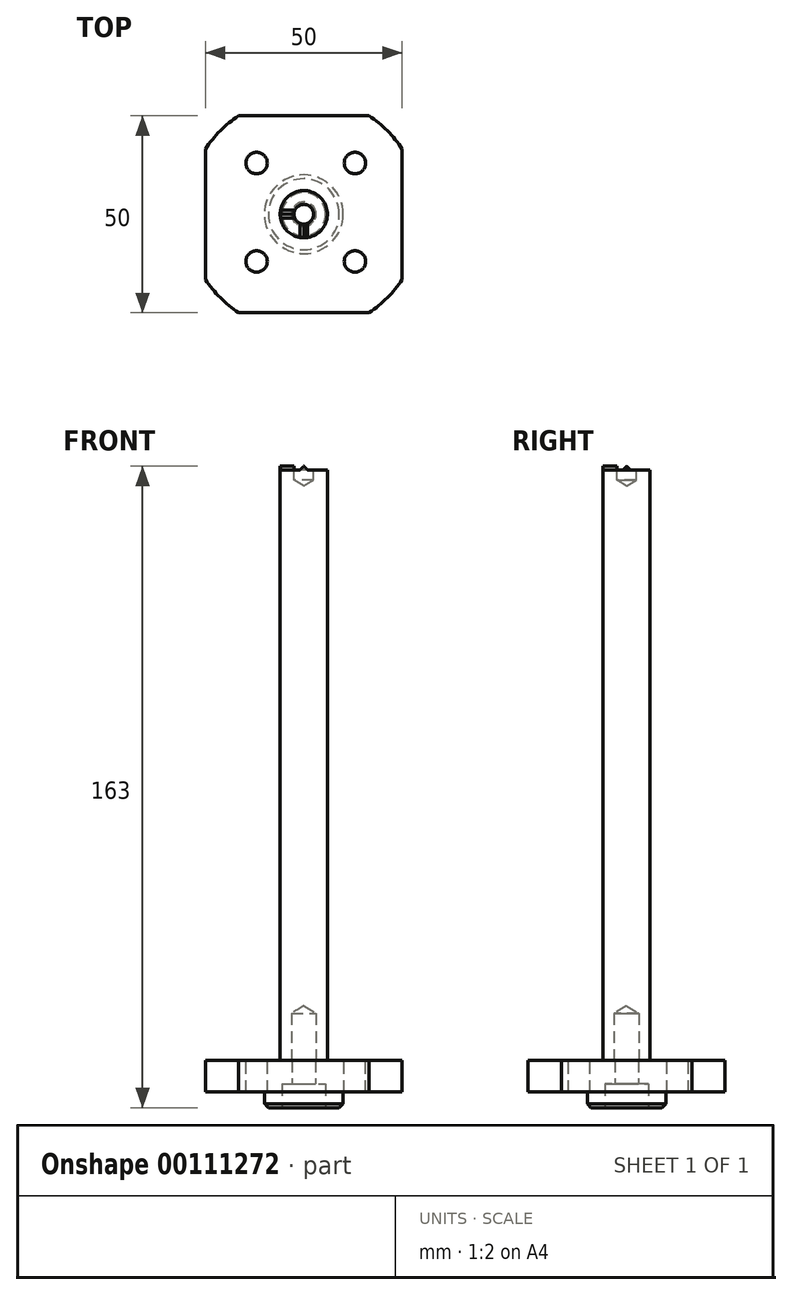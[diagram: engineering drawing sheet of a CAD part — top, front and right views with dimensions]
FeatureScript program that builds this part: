
annotation { "Feature Type Name" : "Feature", "Feature Type Description" : "" }
export const myFeature = defineFeature(function(context is Context, id is Id, definition is map)
    precondition{}
    {
        {
            var Q0;
            Q0=qCreatedBy(makeId("Top.planeOp"),FACE);
            var sketch = newSketch(context, id + "F0", { "sketchPlane" : qUnion([Q0])});
            skLineSegment(sketch, "E0.bottom", {"start": v(-25, 25) * mm, "end": v(25, 25) * mm});
            skLineSegment(sketch, "E0.top", {"start": v(-25, -25) * mm, "end": v(25, -25) * mm});
            skLineSegment(sketch, "E0.left", {"start": v(-25, 25) * mm, "end": v(-25, -25) * mm});
            skLineSegment(sketch, "E0.right", {"start": v(25, 25) * mm, "end": v(25, -25) * mm});
            skLineSegment(sketch, "E1", {"start": v(-25, 25) * mm, "end": v(25, -25) * mm, "construction": true});
            skLineSegment(sketch, "E2", {"start": v(25, 25) * mm, "end": v(-25, -25) * mm, "construction": true});
            skPoint(sketch, "E3", {"position": v(0, 0) * mm});
            skSolve(sketch);
        }
        {
            var Q0;
            Q0=makeQuery(id+"F0.imprint","IMPRINT",FACE,{"disambiguationData":[TD([[makeQuery(id+"F0.imprint","IMPRINT",EDGE,{"derivedFrom":sQuery(id+"F0.wireOp",EDGE,"E0.bottom")}),-1.0]])]});
            extrude(context, id + "F1", {"entities" : qUnion([Q0]), "depth" : 8 * mm});
        }
        {
            var Q0;
            Q0=makeQuery(id+"F1.opExtrude","CAP_FACE",FACE,{"disambiguationData":[OSD([sQuery(id+"F0.wireOp",EDGE,"E0.bottom"),sQuery(id+"F0.wireOp",EDGE,"E0.top"),sQuery(id+"F0.wireOp",EDGE,"E0.left"),sQuery(id+"F0.wireOp",EDGE,"E0.right")])],"isStart":true});
            var sketch = newSketch(context, id + "F2", { "sketchPlane" : qUnion([Q0])});
            skCircle(sketch, "E4", {"center": v(0, 0) * mm, "radius": 10 * mm});
            skSolve(sketch);
        }
        {
            var Q0;
            Q0=makeQuery(id+"F2.imprint","IMPRINT",FACE,{"disambiguationData":[TD([[makeQuery(id+"F2.imprint","IMPRINT",EDGE,{"derivedFrom":sQuery(id+"F2.wireOp",EDGE,"E4")}),1.0]])]});
            extrude(context, id + "F3", {"entities" : qUnion([Q0]), "operationType" : NewBodyOperationType.ADD, "depth" : 4 * mm});
        }
        {
            var Q0;
            Q0=makeQuery(id+"F1.opExtrude","CAP_FACE",FACE,{"disambiguationData":[OSD([sQuery(id+"F0.wireOp",EDGE,"E0.bottom"),sQuery(id+"F0.wireOp",EDGE,"E0.top"),sQuery(id+"F0.wireOp",EDGE,"E0.left"),sQuery(id+"F0.wireOp",EDGE,"E0.right")])],"isStart":false});
            var sketch = newSketch(context, id + "F4", { "sketchPlane" : qUnion([Q0])});
            skCircle(sketch, "E5", {"center": v(0, 0) * mm, "radius": 30 * mm});
            skCircle(sketch, "E6", {"center": v(0, 0) * mm, "radius": 6 * mm});
            skSolve(sketch);
        }
        {
            var Q0;
            {var subQ0=sQuery(id+"F4.wireOp",EDGE,"E5");var subQ1=makeQuery(id+"F1.opExtrude","CAP_EDGE",EDGE,{"disambiguationData":[OSD([sQuery(id+"F0.wireOp",EDGE,"E0.bottom")])],"isStart":false});var subQ2=makeQuery(id+"F4.imprint","INTERSECT",VERTEX,{"disambiguationData":[OD(1.0)],"derivedFrom":[subQ1,subQ0]});Q0=makeQuery(id+"F4.imprint","IMPRINT",FACE,{"disambiguationData":[TD([[makeQuery(id+"F4.imprint","IMPRINT",EDGE,{"disambiguationData":[TD([[subQ2,-1.0]])],"derivedFrom":subQ0}),-1.0]])]});}
            var Q1;
            {var subQ0=sQuery(id+"F4.wireOp",EDGE,"E5");var subQ1=makeQuery(id+"F1.opExtrude","CAP_EDGE",EDGE,{"disambiguationData":[OSD([sQuery(id+"F0.wireOp",EDGE,"E0.bottom")])],"isStart":false});var subQ2=makeQuery(id+"F4.imprint","INTERSECT",VERTEX,{"disambiguationData":[OD(0.0)],"derivedFrom":[subQ1,subQ0]});Q1=makeQuery(id+"F4.imprint","IMPRINT",FACE,{"disambiguationData":[TD([[makeQuery(id+"F4.imprint","IMPRINT",EDGE,{"disambiguationData":[TD([[subQ2,1.0]])],"derivedFrom":subQ0}),-1.0]])]});}
            var Q2;
            {var subQ0=sQuery(id+"F4.wireOp",EDGE,"E5");var subQ1=makeQuery(id+"F1.opExtrude","CAP_EDGE",EDGE,{"disambiguationData":[OSD([sQuery(id+"F0.wireOp",EDGE,"E0.top")])],"isStart":false});var subQ2=makeQuery(id+"F4.imprint","INTERSECT",VERTEX,{"disambiguationData":[OD(1.0)],"derivedFrom":[subQ1,subQ0]});Q2=makeQuery(id+"F4.imprint","IMPRINT",FACE,{"disambiguationData":[TD([[makeQuery(id+"F4.imprint","IMPRINT",EDGE,{"disambiguationData":[TD([[subQ2,-1.0]])],"derivedFrom":subQ0}),-1.0]])]});}
            var Q3;
            {var subQ0=sQuery(id+"F4.wireOp",EDGE,"E5");var subQ1=makeQuery(id+"F1.opExtrude","CAP_EDGE",EDGE,{"disambiguationData":[OSD([sQuery(id+"F0.wireOp",EDGE,"E0.left")])],"isStart":false});var subQ2=makeQuery(id+"F4.imprint","INTERSECT",VERTEX,{"disambiguationData":[OD(1.0)],"derivedFrom":[subQ1,subQ0]});Q3=makeQuery(id+"F4.imprint","IMPRINT",FACE,{"disambiguationData":[TD([[makeQuery(id+"F4.imprint","IMPRINT",EDGE,{"disambiguationData":[TD([[subQ2,-1.0]])],"derivedFrom":subQ0}),-1.0]])]});}
            extrude(context, id + "F5", {"entities" : qUnion([Q0, Q1, Q2, Q3]), "operationType" : NewBodyOperationType.REMOVE, "oppositeDirection" : true, "depth" : 25 * mm});
        }
        {
            var Q0;
            Q0=makeQuery(id+"F4.imprint","IMPRINT",FACE,{"disambiguationData":[TD([[makeQuery(id+"F4.imprint","IMPRINT",EDGE,{"derivedFrom":sQuery(id+"F4.wireOp",EDGE,"E6")}),1.0]])]});
            extrude(context, id + "F6", {"entities" : qUnion([Q0]), "depth" : 150 * mm});
        }
        {
            var Q0;
            Q0=makeQuery(id+"F1.opExtrude","CAP_FACE",FACE,{"disambiguationData":[OSD([sQuery(id+"F0.wireOp",EDGE,"E0.bottom"),sQuery(id+"F0.wireOp",EDGE,"E0.top"),sQuery(id+"F0.wireOp",EDGE,"E0.left"),sQuery(id+"F0.wireOp",EDGE,"E0.right")])],"isStart":false});
            var sketch = newSketch(context, id + "F7", { "sketchPlane" : qUnion([Q0])});
            skCircle(sketch, "E7", {"center": v(13, 13) * mm, "radius": 2.72 * mm});
            skCircle(sketch, "E8.0.1.0", {"center": v(13, -12) * mm, "radius": 2.72 * mm});
            skCircle(sketch, "E8.1.0.0", {"center": v(-12, 13) * mm, "radius": 2.72 * mm});
            skCircle(sketch, "E8.1.1.0", {"center": v(-12, -12) * mm, "radius": 2.72 * mm});
            skLineSegment(sketch, "E8.direction1", {"start": v(13, 13) * mm, "end": v(-12, 13) * mm, "construction": true});
            skLineSegment(sketch, "E8.direction2", {"start": v(13, 13) * mm, "end": v(13, -12) * mm, "construction": true});
            skSolve(sketch);
        }
        {
            var Q0;
            Q0=makeQuery(id+"F7.imprint","IMPRINT",FACE,{"disambiguationData":[TD([[makeQuery(id+"F7.imprint","IMPRINT",EDGE,{"derivedFrom":sQuery(id+"F7.wireOp",EDGE,"E7")}),1.0]])]});
            var Q1;
            Q1=makeQuery(id+"F7.imprint","IMPRINT",FACE,{"disambiguationData":[TD([[makeQuery(id+"F7.imprint","IMPRINT",EDGE,{"derivedFrom":sQuery(id+"F7.wireOp",EDGE,"E8.0.1.0")}),1.0]])]});
            var Q2;
            Q2=makeQuery(id+"F7.imprint","IMPRINT",FACE,{"disambiguationData":[TD([[makeQuery(id+"F7.imprint","IMPRINT",EDGE,{"derivedFrom":sQuery(id+"F7.wireOp",EDGE,"E8.1.1.0")}),1.0]])]});
            var Q3;
            Q3=makeQuery(id+"F7.imprint","IMPRINT",FACE,{"disambiguationData":[TD([[makeQuery(id+"F7.imprint","IMPRINT",EDGE,{"derivedFrom":sQuery(id+"F7.wireOp",EDGE,"E8.1.0.0")}),1.0]])]});
            extrude(context, id + "F8", {"entities" : qUnion([Q0, Q1, Q2, Q3]), "operationType" : NewBodyOperationType.REMOVE, "oppositeDirection" : true, "depth" : 25 * mm});
        }
        {
            var Q0;
            Q0=makeQuery(id+"F3.opExtrude","CAP_EDGE",EDGE,{"disambiguationData":[OSD([sQuery(id+"F2.wireOp",EDGE,"E4")])],"isStart":false});
            chamfer(context, id + "F9", {"entities" : qUnion([Q0]), "width" : 1 * mm, "tangentPropagation" : true});
        }
        {
            var Q0;
            Q0=makeQuery(id+"F3.opExtrude","CAP_FACE",FACE,{"disambiguationData":[OSD([sQuery(id+"F2.wireOp",EDGE,"E4")])],"isStart":false});
            var sketch = newSketch(context, id + "F10", { "sketchPlane" : qUnion([Q0])});
            skCircle(sketch, "E9", {"center": v(0, 0) * mm, "radius": 2.6 * mm});
            skSolve(sketch);
        }
        {
            var Q0;
            Q0=sQuery(id+"F10.wireOp",VERTEX,"E9.center");
            var Q1;
            Q1=makeQuery(id+"F1.opExtrude","SWEPT_BODY",BODY,{"disambiguationData":[OSD([sQuery(id+"F0.wireOp",EDGE,"E0.bottom"),sQuery(id+"F0.wireOp",EDGE,"E0.top"),sQuery(id+"F0.wireOp",EDGE,"E0.left"),sQuery(id+"F0.wireOp",EDGE,"E0.right")])]});
            hole(context, id + "F11", {"style" : HoleStyle.C_BORE, "endStyle" : HoleEndStyle.THROUGH, "holeDiameter" : 6 * mm, "cBoreDiameter" : 11 * mm, "cBoreDepth" : 6 * mm, "locations" : qUnion([Q0]), "scope" : qUnion([Q1]), "isTappedThrough" : true});
        }
        {
            var Q0;
            Q0=sQuery(id+"F4.wireOp",VERTEX,"E5.center");
            var Q1;
            Q1=makeQuery(id+"F6.opExtrude","SWEPT_BODY",BODY,{"disambiguationData":[OSD([sQuery(id+"F4.wireOp",EDGE,"E6")])]});
            hole(context, id + "F12", {"style" : HoleStyle.SIMPLE, "endStyle" : HoleEndStyle.BLIND, "oppositeDirection" : true, "standardTappedOrClearance" : lookupTablePath({ "standard" : "ISO", "fit" : "Close", "size" : "M6", "type" : "Clearance" }), "standardBlindInLast" : lookupTablePath({ "fit" : "Close", "standard" : "ISO", "size" : "M6", "type" : "Clearance" }), "holeDiameter" : 6.3 * mm, "holeDepth" : 12 * mm, "locations" : qUnion([Q0]), "scope" : qUnion([Q1])});
        }
        {
            var Q0;
            Q0=makeQuery(id+"F6.opExtrude","CAP_FACE",FACE,{"disambiguationData":[OSD([sQuery(id+"F4.wireOp",EDGE,"E6")])],"isStart":false});
            var sketch = newSketch(context, id + "F13", { "sketchPlane" : qUnion([Q0])});
            skPoint(sketch, "E10", {"position": v(0, 0) * mm});
            skSolve(sketch);
        }
        {
            var Q0;
            Q0=sQuery(id+"F13.wireOp",VERTEX,"E10");
            var Q1;
            Q1=makeQuery(id+"F6.opExtrude","SWEPT_BODY",BODY,{"disambiguationData":[OSD([sQuery(id+"F4.wireOp",EDGE,"E6")])]});
            hole(context, id + "F14", {"style" : HoleStyle.SIMPLE, "endStyle" : HoleEndStyle.BLIND, "holeDiameter" : 5 * mm, "holeDepth" : 2.5 * mm, "locations" : qUnion([Q0]), "scope" : qUnion([Q1])});
        }
        {
            var Q0;
            Q0=makeQuery(id+"F6.opExtrude","CAP_FACE",FACE,{"disambiguationData":[OSD([sQuery(id+"F4.wireOp",EDGE,"E6")])],"isStart":false});
            var sketch = newSketch(context, id + "F15", { "sketchPlane" : qUnion([Q0])});
            skLineSegment(sketch, "E11", {"start": v(0, 0) * mm, "end": v(-6, 0) * mm, "construction": true});
            skLineSegment(sketch, "E12", {"start": v(0, 0) * mm, "end": v(0, -6) * mm, "construction": true});
            skLineSegment(sketch, "E13.0", {"start": v(0, 1) * mm, "end": v(-6, 1) * mm, "construction": true});
            skLineSegment(sketch, "E14.0", {"start": v(0, -1) * mm, "end": v(-6, -1) * mm, "construction": true});
            skLineSegment(sketch, "E15.0", {"start": v(-1, 0) * mm, "end": v(-1, -6) * mm, "construction": true});
            skLineSegment(sketch, "E16.0", {"start": v(1, 0) * mm, "end": v(1, -6) * mm, "construction": true});
            skPoint(sketch, "E17", {"position": v(-2.3, 1) * mm});
            skPoint(sketch, "E18", {"position": v(-2.3, -1) * mm});
            skPoint(sketch, "E19", {"position": v(-5.92, 1) * mm});
            skPoint(sketch, "E20", {"position": v(-5.92, -1) * mm});
            skLineSegment(sketch, "E21", {"start": v(-5.92, 1) * mm, "end": v(-2.3, 1) * mm});
            skLineSegment(sketch, "E22", {"start": v(-2.3, -1) * mm, "end": v(-5.92, -1) * mm});
            skLineSegment(sketch, "E23", {"start": v(-1, -2.3) * mm, "end": v(-1, -5.92) * mm});
            skLineSegment(sketch, "E24", {"start": v(1, -2.3) * mm, "end": v(1, -5.92) * mm});
            skSolve(sketch);
        }
        {
            var Q0;
            {var subQ0=sQuery(id+"F15.wireOp",EDGE,"E21");Q0=makeQuery(id+"F15.imprint","IMPRINT",FACE,{"disambiguationData":[TD([[makeQuery(id+"F15.imprint","IMPRINT",EDGE,{"derivedFrom":subQ0}),-1.0]])]});}
            var Q1;
            {var subQ0=sQuery(id+"F15.wireOp",EDGE,"E23");Q1=makeQuery(id+"F15.imprint","IMPRINT",FACE,{"disambiguationData":[TD([[makeQuery(id+"F15.imprint","IMPRINT",EDGE,{"derivedFrom":subQ0}),1.0]])]});}
            extrude(context, id + "F16", {"entities" : qUnion([Q0, Q1]), "operationType" : NewBodyOperationType.ADD, "depth" : 1 * mm});
        }
        {
            var Q0;
            Q0=makeQuery(id+"F16.opExtrude","CAP_EDGE",EDGE,{"disambiguationData":[OSD([sQuery(id+"F15.wireOp",EDGE,"E22")])],"isStart":false});
            var Q1;
            Q1=makeQuery(id+"F16.opExtrude","CAP_EDGE",EDGE,{"disambiguationData":[OSD([sQuery(id+"F15.wireOp",EDGE,"E23")])],"isStart":false});
            var Q2;
            Q2=makeQuery(id+"F16.opExtrude","CAP_EDGE",EDGE,{"disambiguationData":[OSD([sQuery(id+"F15.wireOp",EDGE,"E24")])],"isStart":false});
            var Q3;
            Q3=makeQuery(id+"F16.opExtrude","CAP_EDGE",EDGE,{"disambiguationData":[OSD([sQuery(id+"F15.wireOp",EDGE,"E21")])],"isStart":false});
            chamfer(context, id + "F17", {"entities" : qUnion([Q0, Q1, Q2, Q3]), "width" : 1 * mm, "tangentPropagation" : true});
        }
    });
